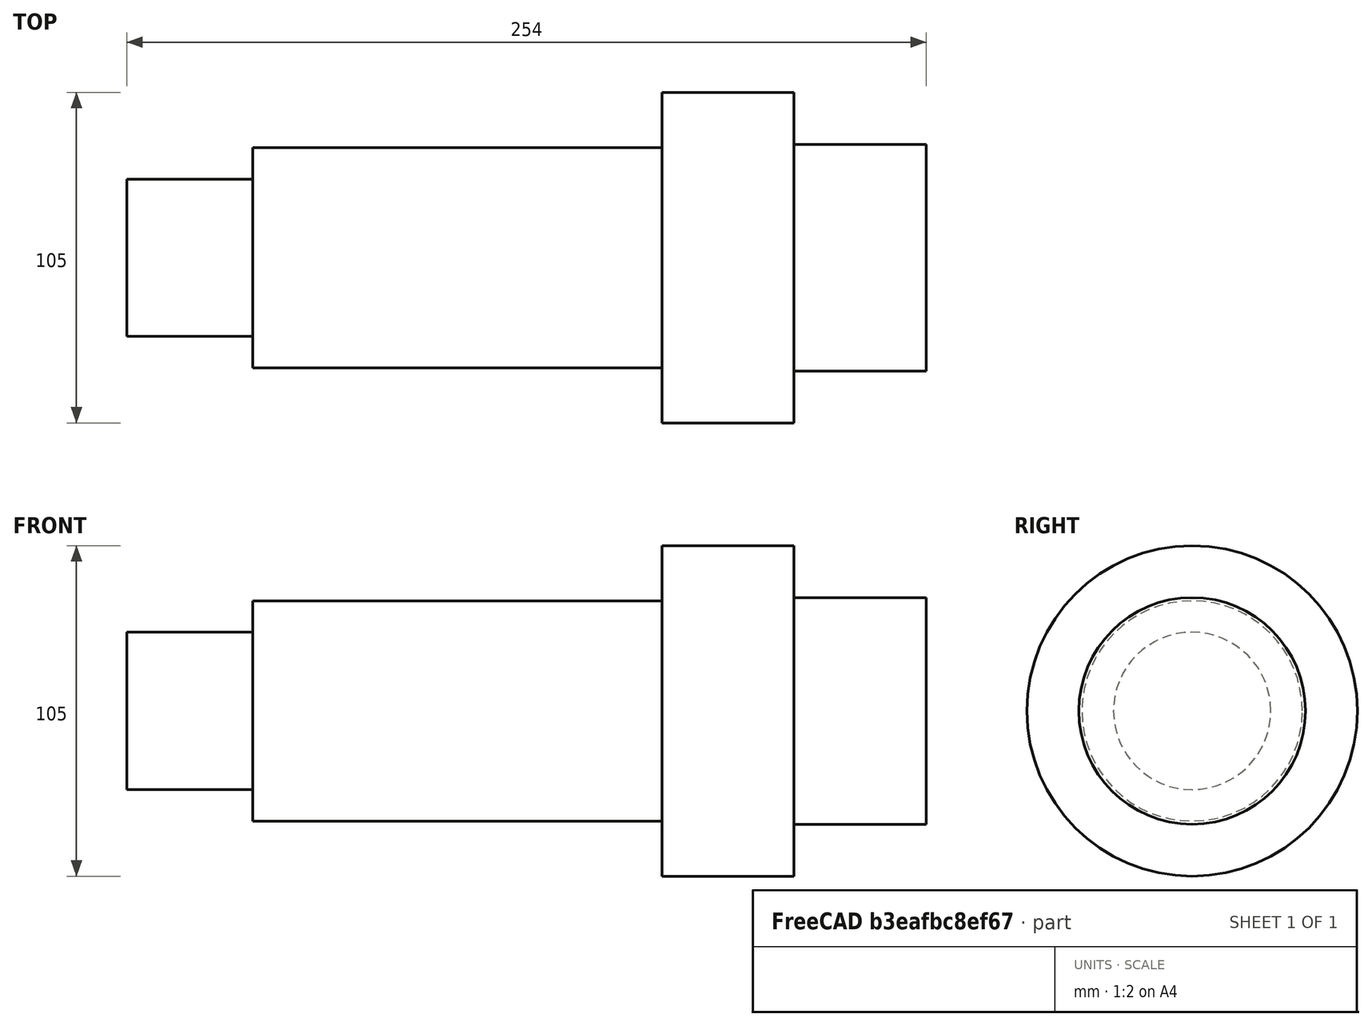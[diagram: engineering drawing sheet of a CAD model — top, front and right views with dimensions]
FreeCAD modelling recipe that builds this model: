
FCSTD DOCUMENT  (FreeCAD 0.21R33771 (Git))
Label: shaftDesigner
License: All rights reserved
LicenseURL: https://en.wikipedia.org/wiki/All_rights_reserved
objects: Sketcher::SketchObject×1, PartDesign::Revolution×1, Fem::ConstraintFixed×1, Fem::ConstraintBearing×1, Fem::ConstraintForce×1
note: 3 computed .brp shape members not serialized (recipe doc carries the construction recipe); baked Part::Feature solids carry a one-line shape summary decoded from their .brp

FEATURE [Sketcher::SketchObject] SketchShaft
  FullyConstrained = true
  sketch-geometry (10):
    g0: LineSegment StartX=9e-16 StartY=0 StartZ=0 EndX=254 EndY=0 EndZ=0
    g1: LineSegment StartX=9e-16 StartY=0 StartZ=0 EndX=9e-16 EndY=25 EndZ=0
    g2: LineSegment StartX=9e-16 StartY=25 StartZ=0 EndX=40 EndY=25 EndZ=0
    g3: LineSegment StartX=40 StartY=25 StartZ=0 EndX=40 EndY=35 EndZ=0
    g4: LineSegment StartX=40 StartY=35 StartZ=0 EndX=170 EndY=35 EndZ=0
    g5: LineSegment StartX=170 StartY=35 StartZ=0 EndX=170 EndY=52.5 EndZ=0
    g6: LineSegment StartX=170 StartY=52.5 StartZ=0 EndX=212 EndY=52.5 EndZ=0
    g7: LineSegment StartX=212 StartY=52.5 StartZ=0 EndX=212 EndY=36 EndZ=0
    g8: LineSegment StartX=212 StartY=36 StartZ=0 EndX=254 EndY=36 EndZ=0
    g9: LineSegment StartX=254 StartY=36 StartZ=0 EndX=254 EndY=0 EndZ=0
  constraints (30):
    c: DistanceX(g0) = 254
    c: DistanceY(g-1,g0) = 0
    c: PointOnObject(g0,g-2)
    c: Horizontal(g0)
    c: DistanceY(g-1,g1) = 25
    c: Coincident(g0,g1)
    c: Vertical(g1)
    c: DistanceX(g2) = 40
    c: Coincident(g2,g1)
    c: Horizontal(g2)
    c: DistanceY(g-1,g3) = 35
    c: Coincident(g3,g2)
    c: Vertical(g3)
    c: DistanceX(g4) = 130
    c: Coincident(g4,g3)
    c: Horizontal(g4)
    c: DistanceY(g-1,g5) = 52.5
    c: Coincident(g5,g4)
    c: Vertical(g5)
    c: DistanceX(g6) = 42
    c: Coincident(g6,g5)
    c: Horizontal(g6)
    c: DistanceY(g-1,g7) = 36
    c: Coincident(g7,g6)
    c: Vertical(g7)
    c: DistanceX(g8) = 42
    c: Coincident(g8,g7)
    c: Horizontal(g8)
    c: Coincident(g0,g9)
    c: Coincident(g9,g8)
FEATURE [PartDesign::Revolution] RevolutionShaft
  Angle = 360
  Axis = (1,0,0)
  Base = (0,0,0)
  Profile = -> SketchShaft
  ReferenceAxis = -> SketchShaft [H_Axis]
FEATURE [Fem::ConstraintFixed] ShaftConstraintFixed
  NormalDirection = (1,0,0)
  Normals = (4) [(1,0,0),(1,0,0),(1,0,0),(1,0,0)]
  Points = (4) [(254,-12,-12),(254,12,-12),(254,-12,12),(254,12,12)]
  References = -> [RevolutionShaft]
  Scale = 8
FEATURE [Fem::ConstraintBearing] ShaftConstraintBearing
  AxialFree = false
  Axis = (1,0,0)
  BasePoint = (191,0,0)
  Dist = 0
  Height = 42
  NormalDirection = (0,-1,1e-16)
  Radius = 52.5
  References = -> [RevolutionShaft]
FEATURE [Fem::ConstraintForce] ShaftConstraintForce
  DirectionVector = (0,0,1)
  Force = 1000
  NormalDirection = (0,0,1)
